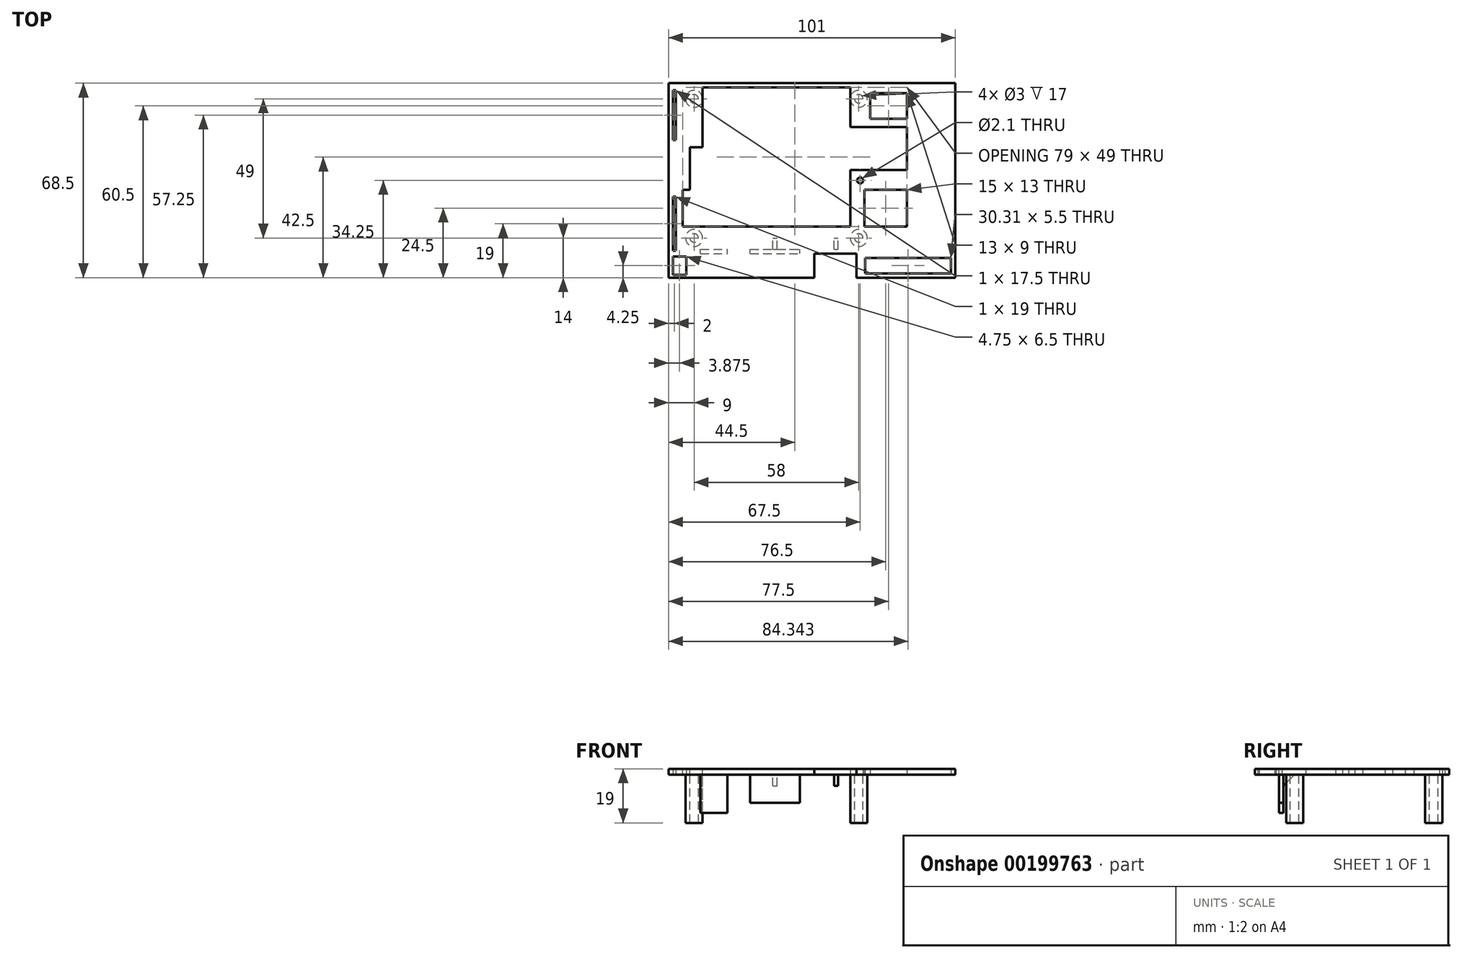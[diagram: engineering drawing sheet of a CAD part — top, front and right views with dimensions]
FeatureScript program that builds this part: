
annotation { "Feature Type Name" : "Feature", "Feature Type Description" : "" }
export const myFeature = defineFeature(function(context is Context, id is Id, definition is map)
    precondition{}
    {
        {
            var Q0;
            Q0=qCreatedBy(makeId("Top.planeOp"),FACE);
            var sketch = newSketch(context, id + "F0", { "sketchPlane" : qUnion([Q0])});
            skLineSegment(sketch, "E0.bottom", {"start": v(0, 0) * mm, "end": v(89, 0) * mm});
            skLineSegment(sketch, "E0.top", {"start": v(0, 60) * mm, "end": v(89, 60) * mm});
            skLineSegment(sketch, "E0.left", {"start": v(0, 0) * mm, "end": v(0, 60) * mm});
            skLineSegment(sketch, "E0.right", {"start": v(89, 0) * mm, "end": v(89, 60) * mm});
            skLineSegment(sketch, "E1", {"start": v(0, 60) * mm, "end": v(-5, 60) * mm});
            skLineSegment(sketch, "E2", {"start": v(-5, 60) * mm, "end": v(-5, 0) * mm});
            skLineSegment(sketch, "E3", {"start": v(-5, 0) * mm, "end": v(-5, -10) * mm});
            skLineSegment(sketch, "E4", {"start": v(-5, -10) * mm, "end": v(89, -10) * mm});
            skLineSegment(sketch, "E5", {"start": v(89, -10) * mm, "end": v(99, -10) * mm});
            skLineSegment(sketch, "E6", {"start": v(99, -10) * mm, "end": v(99, 60) * mm});
            skLineSegment(sketch, "E7", {"start": v(99, 60) * mm, "end": v(89, 60) * mm});
            skLineSegment(sketch, "E8.bottom", {"start": v(-5, 60) * mm, "end": v(99, 60) * mm});
            skLineSegment(sketch, "E8.top", {"start": v(-5, 61.5) * mm, "end": v(99, 61.5) * mm});
            skLineSegment(sketch, "E8.left", {"start": v(-5, 60) * mm, "end": v(-5, 61.5) * mm});
            skLineSegment(sketch, "E8.right", {"start": v(99, 60) * mm, "end": v(99, 61.5) * mm});
            skSolve(sketch);
        }
        {
            var Q0;
            Q0=makeQuery(id+"F0.imprint","IMPRINT",FACE,{"disambiguationData":[TD([[makeQuery(id+"F0.imprint","IMPRINT",EDGE,{"derivedFrom":sQuery(id+"F0.wireOp",EDGE,"E0.bottom")}),-1.0]])]});
            var Q1;
            Q1=makeQuery(id+"F0.imprint","IMPRINT",FACE,{"disambiguationData":[TD([[makeQuery(id+"F0.imprint","IMPRINT",EDGE,{"derivedFrom":sQuery(id+"F0.wireOp",EDGE,"E8.top")}),-1.0]])]});
            var Q2;
            Q2=makeQuery(id+"F0.imprint","IMPRINT",FACE,{"disambiguationData":[TD([[makeQuery(id+"F0.imprint","IMPRINT",EDGE,{"derivedFrom":sQuery(id+"F0.wireOp",EDGE,"E0.bottom")}),1.0]])]});
            extrude(context, id + "F1", {"entities" : qUnion([Q0, Q1, Q2]), "depth" : 2 * mm});
        }
        {
            var Q0;
            Q0=makeQuery(id+"F1.opExtrude","CAP_FACE",FACE,{"disambiguationData":[OSD([sQuery(id+"F0.wireOp",EDGE,"E2"),sQuery(id+"F0.wireOp",EDGE,"E3"),sQuery(id+"F0.wireOp",EDGE,"E4"),sQuery(id+"F0.wireOp",EDGE,"E5"),sQuery(id+"F0.wireOp",EDGE,"E6"),sQuery(id+"F0.wireOp",EDGE,"E8.top"),sQuery(id+"F0.wireOp",EDGE,"E8.left"),sQuery(id+"F0.wireOp",EDGE,"E8.right")])],"isStart":true});
            var sketch = newSketch(context, id + "F2", { "sketchPlane" : qUnion([Q0])});
            skCircle(sketch, "E9", {"center": v(5.5, -5.5) * mm, "radius": 1.5 * mm});
            skCircle(sketch, "E10.0", {"center": v(5.5, -5.5) * mm, "radius": 3 * mm});
            skCircle(sketch, "E11.0.1.0", {"center": v(5.5, -54.5) * mm, "radius": 3 * mm});
            skCircle(sketch, "E11.0.1.1", {"center": v(5.5, -54.5) * mm, "radius": 1.5 * mm});
            skCircle(sketch, "E11.1.0.0", {"center": v(63.5, -5.5) * mm, "radius": 3 * mm});
            skCircle(sketch, "E11.1.0.1", {"center": v(63.5, -5.5) * mm, "radius": 1.5 * mm});
            skCircle(sketch, "E11.1.1.0", {"center": v(63.5, -54.5) * mm, "radius": 3 * mm});
            skCircle(sketch, "E11.1.1.1", {"center": v(63.5, -54.5) * mm, "radius": 1.5 * mm});
            skLineSegment(sketch, "E11.direction1", {"start": v(5.5, -5.5) * mm, "end": v(63.5, -5.5) * mm, "construction": true});
            skLineSegment(sketch, "E11.direction2", {"start": v(5.5, -5.5) * mm, "end": v(5.5, -54.5) * mm, "construction": true});
            skSolve(sketch);
        }
        {
            var Q0;
            Q0=makeQuery(id+"F2.imprint","IMPRINT",FACE,{"disambiguationData":[TD([[makeQuery(id+"F2.imprint","IMPRINT",EDGE,{"derivedFrom":sQuery(id+"F2.wireOp",EDGE,"E9")}),-1.0]])]});
            var Q1;
            Q1=makeQuery(id+"F2.imprint","IMPRINT",FACE,{"disambiguationData":[TD([[makeQuery(id+"F2.imprint","IMPRINT",EDGE,{"derivedFrom":sQuery(id+"F2.wireOp",EDGE,"E11.1.0.0")}),1.0]])]});
            var Q2;
            Q2=makeQuery(id+"F2.imprint","IMPRINT",FACE,{"disambiguationData":[TD([[makeQuery(id+"F2.imprint","IMPRINT",EDGE,{"derivedFrom":sQuery(id+"F2.wireOp",EDGE,"E11.0.1.0")}),1.0]])]});
            var Q3;
            Q3=makeQuery(id+"F2.imprint","IMPRINT",FACE,{"disambiguationData":[TD([[makeQuery(id+"F2.imprint","IMPRINT",EDGE,{"derivedFrom":sQuery(id+"F2.wireOp",EDGE,"E11.1.1.0")}),1.0]])]});
            extrude(context, id + "F3", {"entities" : qUnion([Q0, Q1, Q2, Q3]), "operationType" : NewBodyOperationType.ADD, "depth" : 17 * mm});
        }
        {
            var Q0;
            Q0=makeQuery(id+"F1.opExtrude","CAP_FACE",FACE,{"disambiguationData":[OSD([sQuery(id+"F0.wireOp",EDGE,"E2"),sQuery(id+"F0.wireOp",EDGE,"E3"),sQuery(id+"F0.wireOp",EDGE,"E4"),sQuery(id+"F0.wireOp",EDGE,"E5"),sQuery(id+"F0.wireOp",EDGE,"E6"),sQuery(id+"F0.wireOp",EDGE,"E8.top"),sQuery(id+"F0.wireOp",EDGE,"E8.left"),sQuery(id+"F0.wireOp",EDGE,"E8.right")])],"isStart":false});
            var sketch = newSketch(context, id + "F4", { "sketchPlane" : qUnion([Q0])});
            skLineSegment(sketch, "E12.bottom", {"start": v(8.5, 9.5) * mm, "end": v(60.5, 9.5) * mm});
            skLineSegment(sketch, "E12.top", {"start": v(8.5, 58.5) * mm, "end": v(60.5, 58.5) * mm});
            skLineSegment(sketch, "E12.left", {"start": v(8.5, 9.5) * mm, "end": v(8.5, 58.5) * mm});
            skLineSegment(sketch, "E12.right", {"start": v(60.5, 9.5) * mm, "end": v(60.5, 58.5) * mm});
            skLineSegment(sketch, "E13.bottom", {"start": v(0, 0) * mm, "end": v(89, 0) * mm});
            skLineSegment(sketch, "E13.top", {"start": v(0, 60) * mm, "end": v(89, 60) * mm});
            skLineSegment(sketch, "E13.left", {"start": v(0, 0) * mm, "end": v(0, 60) * mm});
            skLineSegment(sketch, "E13.right", {"start": v(89, 0) * mm, "end": v(89, 60) * mm});
            skSolve(sketch);
        }
        {
            var Q0;
            Q0=makeQuery(id+"F4.imprint","IMPRINT",FACE,{"disambiguationData":[TD([[makeQuery(id+"F4.imprint","IMPRINT",EDGE,{"derivedFrom":sQuery(id+"F4.wireOp",EDGE,"E12.bottom")}),1.0]])]});
            var Q1;
            {var subQ0=sQuery(id+"F0.wireOp",EDGE,"E8.top");var subQ1=sQuery(id+"F0.wireOp",EDGE,"E8.right");var subQ2=sQuery(id+"F0.wireOp",EDGE,"E6");var subQ3=sQuery(id+"F0.wireOp",EDGE,"E5");var subQ4=sQuery(id+"F0.wireOp",EDGE,"E4");var subQ5=sQuery(id+"F0.wireOp",EDGE,"E8.left");var subQ6=sQuery(id+"F0.wireOp",EDGE,"E3");var subQ7=sQuery(id+"F0.wireOp",EDGE,"E2");Q1=makeQuery(id+"F3.boolean.opBoolean","SPLIT",FACE,{"disambiguationData":[TD([makeQuery(id+"F1.opExtrude","SWEPT_FACE",FACE,{"disambiguationData":[OSD([subQ0])]})])],"derivedFrom":makeQuery(id+"F1.opExtrude","CAP_FACE",FACE,{"disambiguationData":[OSD([subQ7,subQ6,subQ4,subQ3,subQ2,subQ0,subQ5,subQ1])],"isStart":true})});}
            extrude(context, id + "F5", {"entities" : qUnion([Q0]), "operationType" : NewBodyOperationType.REMOVE, "endBound" : BoundingType.UP_TO_SURFACE, "oppositeDirection" : true, "endBoundEntityFace" : qUnion([Q1]), "depth" : 25 * mm});
        }
        {
            var Q0;
            Q0=makeQuery(id+"F1.opExtrude","CAP_FACE",FACE,{"disambiguationData":[OSD([sQuery(id+"F0.wireOp",EDGE,"E2"),sQuery(id+"F0.wireOp",EDGE,"E3"),sQuery(id+"F0.wireOp",EDGE,"E4"),sQuery(id+"F0.wireOp",EDGE,"E5"),sQuery(id+"F0.wireOp",EDGE,"E6"),sQuery(id+"F0.wireOp",EDGE,"E8.top"),sQuery(id+"F0.wireOp",EDGE,"E8.left"),sQuery(id+"F0.wireOp",EDGE,"E8.right")])],"isStart":false});
            var sketch = newSketch(context, id + "F6", { "sketchPlane" : qUnion([Q0])});
            skLineSegment(sketch, "E14.bottom", {"start": v(8.5, 37.5) * mm, "end": v(4, 37.5) * mm});
            skLineSegment(sketch, "E14.top", {"start": v(8.5, 22.5) * mm, "end": v(4, 22.5) * mm});
            skLineSegment(sketch, "E14.left", {"start": v(8.5, 37.5) * mm, "end": v(8.5, 22.5) * mm});
            skLineSegment(sketch, "E14.right", {"start": v(4, 37.5) * mm, "end": v(4, 22.5) * mm});
            skLineSegment(sketch, "E15.bottom", {"start": v(8.5, 22.5) * mm, "end": v(1.5, 22.5) * mm});
            skLineSegment(sketch, "E15.top", {"start": v(8.5, 9.5) * mm, "end": v(1.5, 9.5) * mm});
            skLineSegment(sketch, "E15.left", {"start": v(8.5, 22.5) * mm, "end": v(8.5, 9.5) * mm});
            skLineSegment(sketch, "E15.right", {"start": v(1.5, 22.5) * mm, "end": v(1.5, 9.5) * mm});
            skSolve(sketch);
        }
        {
            var Q0;
            Q0=makeQuery(id+"F6.imprint","IMPRINT",FACE,{"disambiguationData":[TD([[makeQuery(id+"F6.imprint","IMPRINT",EDGE,{"derivedFrom":sQuery(id+"F6.wireOp",EDGE,"E14.bottom")}),1.0]])]});
            var Q1;
            Q1=makeQuery(id+"F6.imprint","IMPRINT",FACE,{"disambiguationData":[TD([[makeQuery(id+"F6.imprint","IMPRINT",EDGE,{"derivedFrom":sQuery(id+"F6.wireOp",EDGE,"E15.bottom")}),1.0]])]});
            var Q2;
            {var subQ0=sQuery(id+"F0.wireOp",EDGE,"E8.top");var subQ1=sQuery(id+"F0.wireOp",EDGE,"E8.right");var subQ2=sQuery(id+"F0.wireOp",EDGE,"E6");var subQ3=sQuery(id+"F0.wireOp",EDGE,"E5");var subQ4=sQuery(id+"F0.wireOp",EDGE,"E4");var subQ5=sQuery(id+"F0.wireOp",EDGE,"E8.left");var subQ6=sQuery(id+"F0.wireOp",EDGE,"E3");var subQ7=sQuery(id+"F0.wireOp",EDGE,"E2");Q2=makeQuery(id+"F3.boolean.opBoolean","SPLIT",FACE,{"disambiguationData":[TD([makeQuery(id+"F1.opExtrude","SWEPT_FACE",FACE,{"disambiguationData":[OSD([subQ0])]})])],"derivedFrom":makeQuery(id+"F1.opExtrude","CAP_FACE",FACE,{"disambiguationData":[OSD([subQ7,subQ6,subQ4,subQ3,subQ2,subQ0,subQ5,subQ1])],"isStart":true})});}
            extrude(context, id + "F7", {"entities" : qUnion([Q0, Q1]), "operationType" : NewBodyOperationType.REMOVE, "endBound" : BoundingType.UP_TO_SURFACE, "oppositeDirection" : true, "endBoundEntityFace" : qUnion([Q2]), "depth" : 25 * mm});
        }
        {
            var Q0;
            Q0=makeQuery(id+"F1.opExtrude","CAP_FACE",FACE,{"disambiguationData":[OSD([sQuery(id+"F0.wireOp",EDGE,"E2"),sQuery(id+"F0.wireOp",EDGE,"E3"),sQuery(id+"F0.wireOp",EDGE,"E4"),sQuery(id+"F0.wireOp",EDGE,"E5"),sQuery(id+"F0.wireOp",EDGE,"E6"),sQuery(id+"F0.wireOp",EDGE,"E8.top"),sQuery(id+"F0.wireOp",EDGE,"E8.left"),sQuery(id+"F0.wireOp",EDGE,"E8.right")])],"isStart":false});
            var sketch = newSketch(context, id + "F8", { "sketchPlane" : qUnion([Q0])});
            skLineSegment(sketch, "E16.bottom", {"start": v(47.88, 0) * mm, "end": v(62.69, 0) * mm});
            skLineSegment(sketch, "E16.top", {"start": v(47.88, -15) * mm, "end": v(62.69, -15) * mm});
            skLineSegment(sketch, "E16.left", {"start": v(47.88, 0) * mm, "end": v(47.88, -15) * mm});
            skLineSegment(sketch, "E16.right", {"start": v(62.69, 0) * mm, "end": v(62.69, -15) * mm});
            skSolve(sketch);
        }
        {
            var Q0;
            Q0=makeQuery(id+"F8.imprint","IMPRINT",FACE,{"disambiguationData":[TD([[makeQuery(id+"F8.imprint","IMPRINT",EDGE,{"derivedFrom":sQuery(id+"F8.wireOp",EDGE,"E16.bottom")}),-1.0]])]});
            extrude(context, id + "F9", {"entities" : qUnion([Q0]), "operationType" : NewBodyOperationType.REMOVE, "endBound" : BoundingType.UP_TO_NEXT, "oppositeDirection" : true, "depth" : 25 * mm});
        }
        {
            var Q0;
            Q0=makeQuery(id+"FGdMccBOV7SDvHG_1.boolean.opBoolean","MERGE",EDGE,{"derivedFrom":[makeQuery(id+"F1.opExtrude","SWEPT_EDGE",EDGE,{"disambiguationData":[OSD([sQuery(id+"F0.wireOp",EDGE,"E3"),sQuery(id+"F0.wireOp",EDGE,"E4")])]}),makeQuery(id+"FGdMccBOV7SDvHG_1.opExtrude","CAP_EDGE",EDGE,{"disambiguationData":[OSD([sQuery(id+"FNlEFG9dynNmZq2_1.wireOp",EDGE,"417defb0-fc86-496a-bdf9-6aecbc3ecfc9.0.1")])],"isStart":true})]});
            var Q1;
            Q1=makeQuery(id+"FkCxdxA3eZ6FNy2_1.boolean.opBoolean","MERGE",EDGE,{"derivedFrom":[makeQuery(id+"F1.opExtrude","SWEPT_EDGE",EDGE,{"disambiguationData":[OSD([sQuery(id+"F0.wireOp",EDGE,"E8.top"),sQuery(id+"F0.wireOp",EDGE,"E8.left")])]}),makeQuery(id+"FkCxdxA3eZ6FNy2_1.opExtrude","CAP_EDGE",EDGE,{"disambiguationData":[OSD([sQuery(id+"Fe5vuVaiHyo9jDi_1.wireOp",EDGE,"pEaPp6be-WEG5-MOcO-L7oW-0cAJyYj8UJx9")])],"isStart":true})]});
            var Q2;
            Q2=makeQuery(id+"Fc2HdZ7aDJbILQ9_1.boolean.opBoolean","MERGE",EDGE,{"derivedFrom":[makeQuery(id+"F1.opExtrude","SWEPT_EDGE",EDGE,{"disambiguationData":[OSD([sQuery(id+"F0.wireOp",EDGE,"E5"),sQuery(id+"F0.wireOp",EDGE,"E6")])]}),makeQuery(id+"Fc2HdZ7aDJbILQ9_1.opExtrude","SWEPT_EDGE",EDGE,{"disambiguationData":[OSD([sQuery(id+"FXbliZNcJuKgvEy_1.wireOp",EDGE,"6zkBj3y2-j88h-p4SY-Rkf9-AWoulgX1Fh98.top"),sQuery(id+"FXbliZNcJuKgvEy_1.wireOp",EDGE,"6zkBj3y2-j88h-p4SY-Rkf9-AWoulgX1Fh98.left")])]})]});
            var Q3;
            Q3=makeQuery(id+"Fc2HdZ7aDJbILQ9_1.boolean.opBoolean","MERGE",EDGE,{"derivedFrom":[makeQuery(id+"F1.opExtrude","SWEPT_EDGE",EDGE,{"disambiguationData":[OSD([sQuery(id+"F0.wireOp",EDGE,"E8.top"),sQuery(id+"F0.wireOp",EDGE,"E8.right")])]}),makeQuery(id+"Fc2HdZ7aDJbILQ9_1.opExtrude","SWEPT_EDGE",EDGE,{"disambiguationData":[OSD([sQuery(id+"FXbliZNcJuKgvEy_1.wireOp",EDGE,"6zkBj3y2-j88h-p4SY-Rkf9-AWoulgX1Fh98.bottom"),sQuery(id+"FXbliZNcJuKgvEy_1.wireOp",EDGE,"6zkBj3y2-j88h-p4SY-Rkf9-AWoulgX1Fh98.left")])]})]});
            fillet(context, id + "F10", {"entities" : qUnion([Q0, Q1, Q2, Q3]), "radius" : 2 * mm, "tangentPropagation" : true, "allowEdgeOverflow" : false});
        }
        {
            var Q0;
            {var subQ0=sQuery(id+"F0.wireOp",EDGE,"E8.top");var subQ1=sQuery(id+"F0.wireOp",EDGE,"E8.right");var subQ2=sQuery(id+"F0.wireOp",EDGE,"E6");var subQ3=sQuery(id+"F0.wireOp",EDGE,"E5");var subQ4=sQuery(id+"F0.wireOp",EDGE,"E4");var subQ5=sQuery(id+"F0.wireOp",EDGE,"E8.left");var subQ6=sQuery(id+"F0.wireOp",EDGE,"E3");var subQ7=sQuery(id+"F0.wireOp",EDGE,"E2");Q0=makeQuery(id+"F3.boolean.opBoolean","SPLIT",FACE,{"disambiguationData":[TD([makeQuery(id+"F1.opExtrude","SWEPT_FACE",FACE,{"disambiguationData":[OSD([subQ0])]})])],"derivedFrom":makeQuery(id+"F1.opExtrude","CAP_FACE",FACE,{"disambiguationData":[OSD([subQ7,subQ6,subQ4,subQ3,subQ2,subQ0,subQ5,subQ1])],"isStart":true})});}
            var sketch = newSketch(context, id + "F11", { "sketchPlane" : qUnion([Q0])});
            skLineSegment(sketch, "E17.bottom", {"start": v(25.25, 0) * mm, "end": v(42.75, 0) * mm});
            skLineSegment(sketch, "E17.top", {"start": v(25.25, -1.5) * mm, "end": v(42.75, -1.5) * mm});
            skLineSegment(sketch, "E17.left", {"start": v(25.25, 0) * mm, "end": v(25.25, -1.5) * mm});
            skLineSegment(sketch, "E17.right", {"start": v(42.75, 0) * mm, "end": v(42.75, -1.5) * mm});
            skLineSegment(sketch, "E18.bottom", {"start": v(7.75, 0) * mm, "end": v(17.25, 0) * mm});
            skLineSegment(sketch, "E18.top", {"start": v(7.75, -1.5) * mm, "end": v(17.25, -1.5) * mm});
            skLineSegment(sketch, "E18.left", {"start": v(7.75, 0) * mm, "end": v(7.75, -1.5) * mm});
            skLineSegment(sketch, "E18.right", {"start": v(17.25, 0) * mm, "end": v(17.25, -1.5) * mm});
            skLineSegment(sketch, "E19.bottom", {"start": v(47.88, 0) * mm, "end": v(62.69, 0) * mm});
            skLineSegment(sketch, "E20.bottom", {"start": v(51.5, 0) * mm, "end": v(59.5, 0) * mm});
            skLineSegment(sketch, "E20.top", {"start": v(51.5, -1.5) * mm, "end": v(59.5, -1.5) * mm});
            skLineSegment(sketch, "E20.left", {"start": v(51.5, 0) * mm, "end": v(51.5, -1.5) * mm});
            skLineSegment(sketch, "E20.right", {"start": v(59.5, 0) * mm, "end": v(59.5, -1.5) * mm});
            skSolve(sketch);
        }
        {
            var Q0;
            Q0=makeQuery(id+"F11.imprint","IMPRINT",FACE,{"disambiguationData":[TD([[makeQuery(id+"F11.imprint","IMPRINT",EDGE,{"derivedFrom":sQuery(id+"F11.wireOp",EDGE,"E17.bottom")}),-1.0]])]});
            var Q1;
            Q1=makeQuery(id+"F11.imprint","IMPRINT",FACE,{"disambiguationData":[TD([[makeQuery(id+"F11.imprint","IMPRINT",EDGE,{"derivedFrom":sQuery(id+"F11.wireOp",EDGE,"E20.bottom")}),1.0]])]});
            extrude(context, id + "F12", {"entities" : qUnion([Q0, Q1]), "operationType" : NewBodyOperationType.ADD, "depth" : 10 * mm});
        }
        {
            var Q0;
            Q0=makeQuery(id+"F11.imprint","IMPRINT",FACE,{"disambiguationData":[TD([[makeQuery(id+"F11.imprint","IMPRINT",EDGE,{"derivedFrom":sQuery(id+"F11.wireOp",EDGE,"E18.bottom")}),-1.0]])]});
            extrude(context, id + "F13", {"entities" : qUnion([Q0]), "operationType" : NewBodyOperationType.ADD, "depth" : 13.5 * mm});
        }
        {
            var Q0;
            Q0=makeQuery(id+"F11.imprint","IMPRINT",FACE,{"disambiguationData":[TD([[makeQuery(id+"F11.imprint","IMPRINT",EDGE,{"derivedFrom":sQuery(id+"F11.wireOp",EDGE,"E17.bottom")}),1.0]])]});
            var sketch = newSketch(context, id + "F14", { "sketchPlane" : qUnion([Q0])});
            skLineSegment(sketch, "E21.0", {"start": v(7.75, -1.5) * mm, "end": v(17.25, -1.5) * mm});
            skLineSegment(sketch, "E22.bottom", {"start": v(11.75, -1.5) * mm, "end": v(13.25, -1.5) * mm});
            skLineSegment(sketch, "E22.top", {"start": v(11.75, -5.5) * mm, "end": v(13.25, -5.5) * mm});
            skLineSegment(sketch, "E22.left", {"start": v(11.75, -1.5) * mm, "end": v(11.75, -5.5) * mm});
            skLineSegment(sketch, "E22.right", {"start": v(13.25, -1.5) * mm, "end": v(13.25, -5.5) * mm});
            skPoint(sketch, "E23", {"position": v(12.5, -1.5) * mm});
            skLineSegment(sketch, "E24.bottom", {"start": v(33.25, -1.5) * mm, "end": v(34.75, -1.5) * mm});
            skLineSegment(sketch, "E24.top", {"start": v(33.25, -5.5) * mm, "end": v(34.75, -5.5) * mm});
            skLineSegment(sketch, "E24.left", {"start": v(33.25, -1.5) * mm, "end": v(33.25, -5.5) * mm});
            skLineSegment(sketch, "E24.right", {"start": v(34.75, -1.5) * mm, "end": v(34.75, -5.5) * mm});
            skLineSegment(sketch, "E25.bottom", {"start": v(54.75, -1.5) * mm, "end": v(56.25, -1.5) * mm});
            skLineSegment(sketch, "E25.top", {"start": v(54.75, -5.5) * mm, "end": v(56.25, -5.5) * mm});
            skLineSegment(sketch, "E25.left", {"start": v(54.75, -1.5) * mm, "end": v(54.75, -5.5) * mm});
            skLineSegment(sketch, "E25.right", {"start": v(56.25, -1.5) * mm, "end": v(56.25, -5.5) * mm});
            skSolve(sketch);
        }
        {
            var Q0;
            Q0=makeQuery(id+"F14.imprint","IMPRINT",FACE,{"disambiguationData":[TD([[makeQuery(id+"F14.imprint","IMPRINT",EDGE,{"derivedFrom":sQuery(id+"F14.wireOp",EDGE,"E24.bottom")}),-1.0]])]});
            var Q1;
            Q1=makeQuery(id+"F14.imprint","IMPRINT",FACE,{"disambiguationData":[TD([[makeQuery(id+"F14.imprint","IMPRINT",EDGE,{"derivedFrom":sQuery(id+"F14.wireOp",EDGE,"E25.bottom")}),-1.0]])]});
            var Q2;
            Q2=makeQuery(id+"F14.imprint","IMPRINT",FACE,{"disambiguationData":[TD([[makeQuery(id+"F14.imprint","IMPRINT",EDGE,{"derivedFrom":sQuery(id+"F14.wireOp",EDGE,"E22.bottom")}),-1.0]])]});
            extrude(context, id + "F15", {"entities" : qUnion([Q0, Q1, Q2]), "operationType" : NewBodyOperationType.ADD, "depth" : 4 * mm});
        }
        {
            var Q0;
            Q0=makeQuery(id+"F15.opExtrude","CAP_EDGE",EDGE,{"disambiguationData":[OSD([sQuery(id+"F14.wireOp",EDGE,"E22.top")])],"isStart":false});
            var Q1;
            Q1=makeQuery(id+"F15.opExtrude","CAP_EDGE",EDGE,{"disambiguationData":[OSD([sQuery(id+"F14.wireOp",EDGE,"E24.top")])],"isStart":false});
            var Q2;
            Q2=makeQuery(id+"F15.opExtrude","CAP_EDGE",EDGE,{"disambiguationData":[OSD([sQuery(id+"F14.wireOp",EDGE,"E25.top")])],"isStart":false});
            chamfer(context, id + "F16", {"entities" : qUnion([Q0, Q1, Q2]), "width" : 4 * mm, "tangentPropagation" : true});
        }
        {
            var Q0;
            {var subQ0=sQuery(id+"F0.wireOp",EDGE,"E8.top");var subQ1=sQuery(id+"F0.wireOp",EDGE,"E8.right");var subQ2=sQuery(id+"F0.wireOp",EDGE,"E6");var subQ3=sQuery(id+"F0.wireOp",EDGE,"E5");var subQ4=sQuery(id+"F0.wireOp",EDGE,"E4");var subQ5=sQuery(id+"F0.wireOp",EDGE,"E8.left");var subQ6=sQuery(id+"F0.wireOp",EDGE,"E3");var subQ7=sQuery(id+"F0.wireOp",EDGE,"E2");Q0=makeQuery(id+"F3.boolean.opBoolean","SPLIT",FACE,{"disambiguationData":[TD([makeQuery(id+"F1.opExtrude","SWEPT_FACE",FACE,{"disambiguationData":[OSD([subQ0])]})])],"derivedFrom":makeQuery(id+"F1.opExtrude","CAP_FACE",FACE,{"disambiguationData":[OSD([subQ7,subQ6,subQ4,subQ3,subQ2,subQ0,subQ5,subQ1])],"isStart":true})});}
            var sketch = newSketch(context, id + "F17", { "sketchPlane" : qUnion([Q0])});
            skLineSegment(sketch, "E26.bottom", {"start": v(60.5, -29.5) * mm, "end": v(80.5, -29.5) * mm});
            skLineSegment(sketch, "E26.top", {"start": v(60.5, -44.5) * mm, "end": v(80.5, -44.5) * mm});
            skLineSegment(sketch, "E26.left", {"start": v(60.5, -29.5) * mm, "end": v(60.5, -44.5) * mm});
            skLineSegment(sketch, "E26.right", {"start": v(80.5, -29.5) * mm, "end": v(80.5, -44.5) * mm});
            skSolve(sketch);
        }
        {
            var Q0;
            Q0=makeQuery(id+"F17.imprint","IMPRINT",FACE,{"disambiguationData":[TD([[makeQuery(id+"F17.imprint","IMPRINT",EDGE,{"derivedFrom":sQuery(id+"F17.wireOp",EDGE,"E26.bottom")}),-1.0]])]});
            extrude(context, id + "F18", {"entities" : qUnion([Q0]), "operationType" : NewBodyOperationType.REMOVE, "endBound" : BoundingType.UP_TO_NEXT, "oppositeDirection" : true, "depth" : 25 * mm});
        }
        {
            var Q0;
            {var subQ0=sQuery(id+"F0.wireOp",EDGE,"E8.top");var subQ1=sQuery(id+"F0.wireOp",EDGE,"E8.right");var subQ2=sQuery(id+"F0.wireOp",EDGE,"E6");var subQ3=sQuery(id+"F0.wireOp",EDGE,"E5");var subQ4=sQuery(id+"F0.wireOp",EDGE,"E4");var subQ5=sQuery(id+"F0.wireOp",EDGE,"E8.left");var subQ6=sQuery(id+"F0.wireOp",EDGE,"E3");var subQ7=sQuery(id+"F0.wireOp",EDGE,"E2");Q0=makeQuery(id+"F3.boolean.opBoolean","SPLIT",FACE,{"disambiguationData":[TD([makeQuery(id+"F1.opExtrude","SWEPT_FACE",FACE,{"disambiguationData":[OSD([subQ0])]})])],"derivedFrom":makeQuery(id+"F1.opExtrude","CAP_FACE",FACE,{"disambiguationData":[OSD([subQ7,subQ6,subQ4,subQ3,subQ2,subQ0,subQ5,subQ1])],"isStart":true})});}
            var sketch = newSketch(context, id + "F19", { "sketchPlane" : qUnion([Q0])});
            skLineSegment(sketch, "E27.0.0", {"start": v(47.88, 10) * mm, "end": v(-3, 10) * mm});
            skArc(sketch, "E27.0.1", {"start": v(-3, 10) * mm, "mid": v(-4.41, 9.41) * mm, "end": v(-5, 8) * mm});
            skLineSegment(sketch, "E27.0.2", {"start": v(-5, 8) * mm, "end": v(-5, -59.5) * mm});
            skArc(sketch, "E27.0.3", {"start": v(-5, -59.5) * mm, "mid": v(-4.41, -60.91) * mm, "end": v(-3, -61.5) * mm});
            skLineSegment(sketch, "E27.0.4", {"start": v(-3, -61.5) * mm, "end": v(97, -61.5) * mm});
            skArc(sketch, "E27.0.5", {"start": v(97, -61.5) * mm, "mid": v(98.41, -60.91) * mm, "end": v(99, -59.5) * mm});
            skLineSegment(sketch, "E27.0.6", {"start": v(99, -59.5) * mm, "end": v(99, 8) * mm});
            skArc(sketch, "E27.0.7", {"start": v(99, 8) * mm, "mid": v(98.66, 9.1) * mm, "end": v(97.77, 9.85) * mm});
            skLineSegment(sketch, "E28.bottom", {"start": v(65.5, -22.5) * mm, "end": v(80.5, -22.5) * mm});
            skLineSegment(sketch, "E28.top", {"start": v(65.5, -9.5) * mm, "end": v(80.5, -9.5) * mm});
            skLineSegment(sketch, "E28.left", {"start": v(65.5, -22.5) * mm, "end": v(65.5, -9.5) * mm});
            skLineSegment(sketch, "E28.right", {"start": v(80.5, -22.5) * mm, "end": v(80.5, -9.5) * mm});
            skLineSegment(sketch, "E29.bottom", {"start": v(67.5, -47.5) * mm, "end": v(80.5, -47.5) * mm});
            skLineSegment(sketch, "E29.top", {"start": v(67.5, -56.5) * mm, "end": v(80.5, -56.5) * mm});
            skLineSegment(sketch, "E29.left", {"start": v(67.5, -47.5) * mm, "end": v(67.5, -56.5) * mm});
            skLineSegment(sketch, "E29.right", {"start": v(80.5, -47.5) * mm, "end": v(80.5, -56.5) * mm});
            skLineSegment(sketch, "E30.bottom", {"start": v(62.69, 10) * mm, "end": v(99, 10) * mm});
            skLineSegment(sketch, "E30.top", {"start": v(62.69, -1.5) * mm, "end": v(99, -1.5) * mm});
            skLineSegment(sketch, "E30.left", {"start": v(62.69, 10) * mm, "end": v(62.69, -1.5) * mm});
            skLineSegment(sketch, "E30.right", {"start": v(99, 10) * mm, "end": v(99, -1.5) * mm});
            skLineSegment(sketch, "E31.bottom", {"start": v(65.69, 7) * mm, "end": v(96, 7) * mm});
            skLineSegment(sketch, "E31.top", {"start": v(65.69, 1.5) * mm, "end": v(96, 1.5) * mm});
            skLineSegment(sketch, "E31.left", {"start": v(65.69, 7) * mm, "end": v(65.69, 1.5) * mm});
            skLineSegment(sketch, "E31.right", {"start": v(96, 7) * mm, "end": v(96, 1.5) * mm});
            skSolve(sketch);
        }
        {
            var Q0;
            Q0=makeQuery(id+"F19.imprint","IMPRINT",FACE,{"disambiguationData":[TD([[makeQuery(id+"F19.imprint","IMPRINT",EDGE,{"derivedFrom":sQuery(id+"F19.wireOp",EDGE,"E28.bottom")}),1.0]])]});
            var Q1;
            Q1=makeQuery(id+"F19.imprint","IMPRINT",FACE,{"disambiguationData":[TD([[makeQuery(id+"F19.imprint","IMPRINT",EDGE,{"derivedFrom":sQuery(id+"F19.wireOp",EDGE,"E31.bottom")}),-1.0]])]});
            var Q2;
            Q2=makeQuery(id+"F19.imprint","IMPRINT",FACE,{"disambiguationData":[TD([[makeQuery(id+"F19.imprint","IMPRINT",EDGE,{"derivedFrom":sQuery(id+"F19.wireOp",EDGE,"E29.bottom")}),-1.0]])]});
            var Q3;
            {var subQ1=sQuery(id+"F0.wireOp",EDGE,"E8.top");var subQ2=sQuery(id+"F0.wireOp",EDGE,"E5");var subQ3=sQuery(id+"F0.wireOp",EDGE,"E4");Q3=makeQuery(id+"FxiqLfpHTpMkQBt_1.boolean.opBoolean","SPLIT",FACE,{"disambiguationData":[TD([makeQuery(id+"F5.boolean.opBoolean","COPY",FACE,{"derivedFrom":makeQuery(id+"F5.opExtrude","SWEPT_FACE",FACE,{"disambiguationData":[OSD([sQuery(id+"F4.wireOp",EDGE,"E12.bottom")])]})})])],"derivedFrom":makeQuery(id+"F1.opExtrude","CAP_FACE",FACE,{"disambiguationData":[OSD([sQuery(id+"F0.wireOp",EDGE,"E2"),sQuery(id+"F0.wireOp",EDGE,"E3"),subQ3,subQ2,sQuery(id+"F0.wireOp",EDGE,"E6"),subQ1,sQuery(id+"F0.wireOp",EDGE,"E8.left"),sQuery(id+"F0.wireOp",EDGE,"E8.right")])],"isStart":false})});}
            extrude(context, id + "F20", {"entities" : qUnion([Q0, Q1, Q2]), "operationType" : NewBodyOperationType.REMOVE, "endBound" : BoundingType.UP_TO_SURFACE, "oppositeDirection" : true, "endBoundEntityFace" : qUnion([Q3]), "depth" : 25 * mm});
        }
        {
            var Q0;
            Q0=makeQuery(id+"F1.opExtrude","CAP_FACE",FACE,{"disambiguationData":[OSD([sQuery(id+"F0.wireOp",EDGE,"E2"),sQuery(id+"F0.wireOp",EDGE,"E3"),sQuery(id+"F0.wireOp",EDGE,"E4"),sQuery(id+"F0.wireOp",EDGE,"E5"),sQuery(id+"F0.wireOp",EDGE,"E6"),sQuery(id+"F0.wireOp",EDGE,"E8.top"),sQuery(id+"F0.wireOp",EDGE,"E8.left"),sQuery(id+"F0.wireOp",EDGE,"E8.right")])],"isStart":false});
            var sketch = newSketch(context, id + "F21", { "sketchPlane" : qUnion([Q0])});
            skCircle(sketch, "E32", {"center": v(44, 14.5) * mm, "radius": 1.05 * mm});
            skCircle(sketch, "E33", {"center": v(64, 25.75) * mm, "radius": 1.05 * mm});
            skLineSegment(sketch, "E34", {"start": v(64, 25.75) * mm, "end": v(64, -10) * mm});
            skLineSegment(sketch, "E35", {"start": v(64, 25.75) * mm, "end": v(64, 61.5) * mm});
            skSolve(sketch);
        }
        {
            var Q0;
            Q0=makeQuery(id+"F0.imprint","IMPRINT",FACE,{"disambiguationData":[TD([[makeQuery(id+"F0.imprint","IMPRINT",EDGE,{"derivedFrom":sQuery(id+"F0.wireOp",EDGE,"E0.bottom")}),-1.0]])]});
            var sketch = newSketch(context, id + "F22", { "sketchPlane" : qUnion([Q0])});
            skLineSegment(sketch, "E36.bottom", {"start": v(-2, 57.5) * mm, "end": v(-1, 57.5) * mm});
            skLineSegment(sketch, "E36.top", {"start": v(-2, 40) * mm, "end": v(-1, 40) * mm});
            skLineSegment(sketch, "E36.left", {"start": v(-2, 57.5) * mm, "end": v(-2, 40) * mm});
            skLineSegment(sketch, "E36.right", {"start": v(-1, 57.5) * mm, "end": v(-1, 40) * mm});
            skLineSegment(sketch, "E37.bottom", {"start": v(-2, 20) * mm, "end": v(-1, 20) * mm});
            skLineSegment(sketch, "E37.top", {"start": v(-2, 1) * mm, "end": v(-1, 1) * mm});
            skLineSegment(sketch, "E37.left", {"start": v(-2, 20) * mm, "end": v(-2, 1) * mm});
            skLineSegment(sketch, "E37.right", {"start": v(-1, 20) * mm, "end": v(-1, 1) * mm});
            skLineSegment(sketch, "E38.bottom", {"start": v(2.75, -1) * mm, "end": v(-2, -1) * mm});
            skLineSegment(sketch, "E38.top", {"start": v(2.75, -7.5) * mm, "end": v(-2, -7.5) * mm});
            skLineSegment(sketch, "E38.left", {"start": v(2.75, -1) * mm, "end": v(2.75, -7.5) * mm});
            skLineSegment(sketch, "E38.right", {"start": v(-2, -1) * mm, "end": v(-2, -7.5) * mm});
            skSolve(sketch);
        }
        {
            var Q0;
            Q0=makeQuery(id+"F22.imprint","IMPRINT",FACE,{"disambiguationData":[TD([[makeQuery(id+"F22.imprint","IMPRINT",EDGE,{"derivedFrom":sQuery(id+"F22.wireOp",EDGE,"E38.bottom")}),1.0]])]});
            var Q1;
            Q1=makeQuery(id+"F22.imprint","IMPRINT",FACE,{"disambiguationData":[TD([[makeQuery(id+"F22.imprint","IMPRINT",EDGE,{"derivedFrom":sQuery(id+"F22.wireOp",EDGE,"E37.bottom")}),-1.0]])]});
            var Q2;
            Q2=makeQuery(id+"F22.imprint","IMPRINT",FACE,{"disambiguationData":[TD([[makeQuery(id+"F22.imprint","IMPRINT",EDGE,{"derivedFrom":sQuery(id+"F22.wireOp",EDGE,"E36.bottom")}),-1.0]])]});
            extrude(context, id + "F23", {"entities" : qUnion([Q0, Q1, Q2]), "operationType" : NewBodyOperationType.REMOVE, "endBound" : BoundingType.UP_TO_NEXT, "depth" : 25 * mm});
        }
        {
            var Q0;
            Q0=makeQuery(id+"F1.opExtrude","CAP_FACE",FACE,{"disambiguationData":[OSD([sQuery(id+"F0.wireOp",EDGE,"E2"),sQuery(id+"F0.wireOp",EDGE,"E3"),sQuery(id+"F0.wireOp",EDGE,"E4"),sQuery(id+"F0.wireOp",EDGE,"E5"),sQuery(id+"F0.wireOp",EDGE,"E6"),sQuery(id+"F0.wireOp",EDGE,"E8.top"),sQuery(id+"F0.wireOp",EDGE,"E8.left"),sQuery(id+"F0.wireOp",EDGE,"E8.right")])],"isStart":false});
            var sketch = newSketch(context, id + "F24", { "sketchPlane" : qUnion([Q0])});
            skLineSegment(sketch, "E39.bottom", {"start": v(-3.5, 60) * mm, "end": v(97.5, 60) * mm});
            skLineSegment(sketch, "E39.top", {"start": v(-3.5, -8.5) * mm, "end": v(97.5, -8.5) * mm});
            skLineSegment(sketch, "E39.left", {"start": v(-3.5, 60) * mm, "end": v(-3.5, -8.5) * mm});
            skLineSegment(sketch, "E39.right", {"start": v(97.5, 60) * mm, "end": v(97.5, -8.5) * mm});
            skSolve(sketch);
        }
        {
            var Q0;
            Q0=makeQuery(id+"F24.imprint","IMPRINT",FACE,{"disambiguationData":[TD([[makeQuery(id+"F24.imprint","IMPRINT",EDGE,{"derivedFrom":sQuery(id+"F24.wireOp",EDGE,"E39.bottom")}),1.0]])]});
            extrude(context, id + "F25", {"entities" : qUnion([Q0]), "operationType" : NewBodyOperationType.REMOVE, "endBound" : BoundingType.UP_TO_NEXT, "oppositeDirection" : true, "depth" : 25 * mm});
        }
        {
            var Q0;
            {var subQ0=sQuery(id+"F21.wireOp",EDGE,"E34");var subQ1=sQuery(id+"F21.wireOp",EDGE,"E33");var subQ2=makeQuery(id+"F21.imprint","INTERSECT",VERTEX,{"derivedFrom":[subQ1,subQ0]});Q0=makeQuery(id+"F21.imprint","IMPRINT",FACE,{"disambiguationData":[TD([[makeQuery(id+"F21.imprint","IMPRINT",EDGE,{"disambiguationData":[TD([[subQ2,-1.0]])],"derivedFrom":subQ1}),1.0]])]});}
            var Q1;
            {var subQ0=sQuery(id+"F21.wireOp",EDGE,"E34");var subQ1=sQuery(id+"F21.wireOp",EDGE,"E33");var subQ2=makeQuery(id+"F21.imprint","INTERSECT",VERTEX,{"derivedFrom":[subQ1,subQ0]});Q1=makeQuery(id+"F21.imprint","IMPRINT",FACE,{"disambiguationData":[TD([[makeQuery(id+"F21.imprint","IMPRINT",EDGE,{"disambiguationData":[TD([[subQ2,1.0]])],"derivedFrom":subQ1}),1.0]])]});}
            var Q2;
            Q2=makeQuery(id+"F21.imprint","IMPRINT",FACE,{"disambiguationData":[TD([[makeQuery(id+"F21.imprint","IMPRINT",EDGE,{"derivedFrom":sQuery(id+"F21.wireOp",EDGE,"E32")}),1.0]])]});
            var Q3;
            {var subQ0=sQuery(id+"F0.wireOp",EDGE,"E8.top");var subQ1=sQuery(id+"F0.wireOp",EDGE,"E8.right");var subQ2=sQuery(id+"F0.wireOp",EDGE,"E6");var subQ3=sQuery(id+"F0.wireOp",EDGE,"E5");var subQ4=sQuery(id+"F0.wireOp",EDGE,"E4");var subQ5=sQuery(id+"F0.wireOp",EDGE,"E8.left");var subQ6=sQuery(id+"F0.wireOp",EDGE,"E3");var subQ7=sQuery(id+"F0.wireOp",EDGE,"E2");Q3=makeQuery(id+"F3.boolean.opBoolean","SPLIT",FACE,{"disambiguationData":[TD([makeQuery(id+"F1.opExtrude","SWEPT_FACE",FACE,{"disambiguationData":[OSD([subQ0])]})])],"derivedFrom":makeQuery(id+"F1.opExtrude","CAP_FACE",FACE,{"disambiguationData":[OSD([subQ7,subQ6,subQ4,subQ3,subQ2,subQ0,subQ5,subQ1])],"isStart":true})});}
            extrude(context, id + "F26", {"entities" : qUnion([Q0, Q1, Q2]), "operationType" : NewBodyOperationType.REMOVE, "endBound" : BoundingType.UP_TO_SURFACE, "oppositeDirection" : true, "endBoundEntityFace" : qUnion([Q3]), "depth" : 25 * mm});
        }
    });
